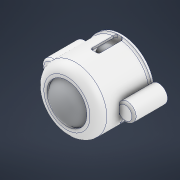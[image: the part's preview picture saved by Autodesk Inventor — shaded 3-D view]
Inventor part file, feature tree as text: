
AUTODESK INVENTOR PART (.ipt)
format: ipt  version: 2021 (Build 250183000, 183)  size: 483,840 bytes
history: mixed  units: mm
features: delete_face x4, revolve x4, fillet x1, imported_body x1
ambient origin geometry x8: Origin, YZ Plane, XZ Plane, XY Plane, X Axis, Y Axis, Z Axis, Center Point
bodies: Solid1 (imported_parasolid), Solid2 (imported_parasolid), Solid3 (imported_parasolid), Solid4 (imported_parasolid), Solid5 (imported_parasolid)
feature tree (10):
  delete_face  "Delete Face1"
  delete_face  "Delete Face2"
  delete_face  "Delete Face3"
  delete_face  "Delete Face4"
  revolve  "Revolve1"  [1 undecoded]
  revolve  "Revolve2"  [1 undecoded]
  revolve  "Revolve3"  [1 undecoded]
  revolve  "Revolve4"  [1 undecoded]
  fillet  "Fillet6"  [1 undecoded]
  imported_body  NMx_Import_Brep_tag  [imported B-rep: ~29 faces, bbox_mm=[21.8, 3.32997, 11.0]]
note: 5 required parameter values undecoded (feature->parameter linkage not recoverable at this tier; creation-order binding heuristic only, values carry confidence <= 0.55)
